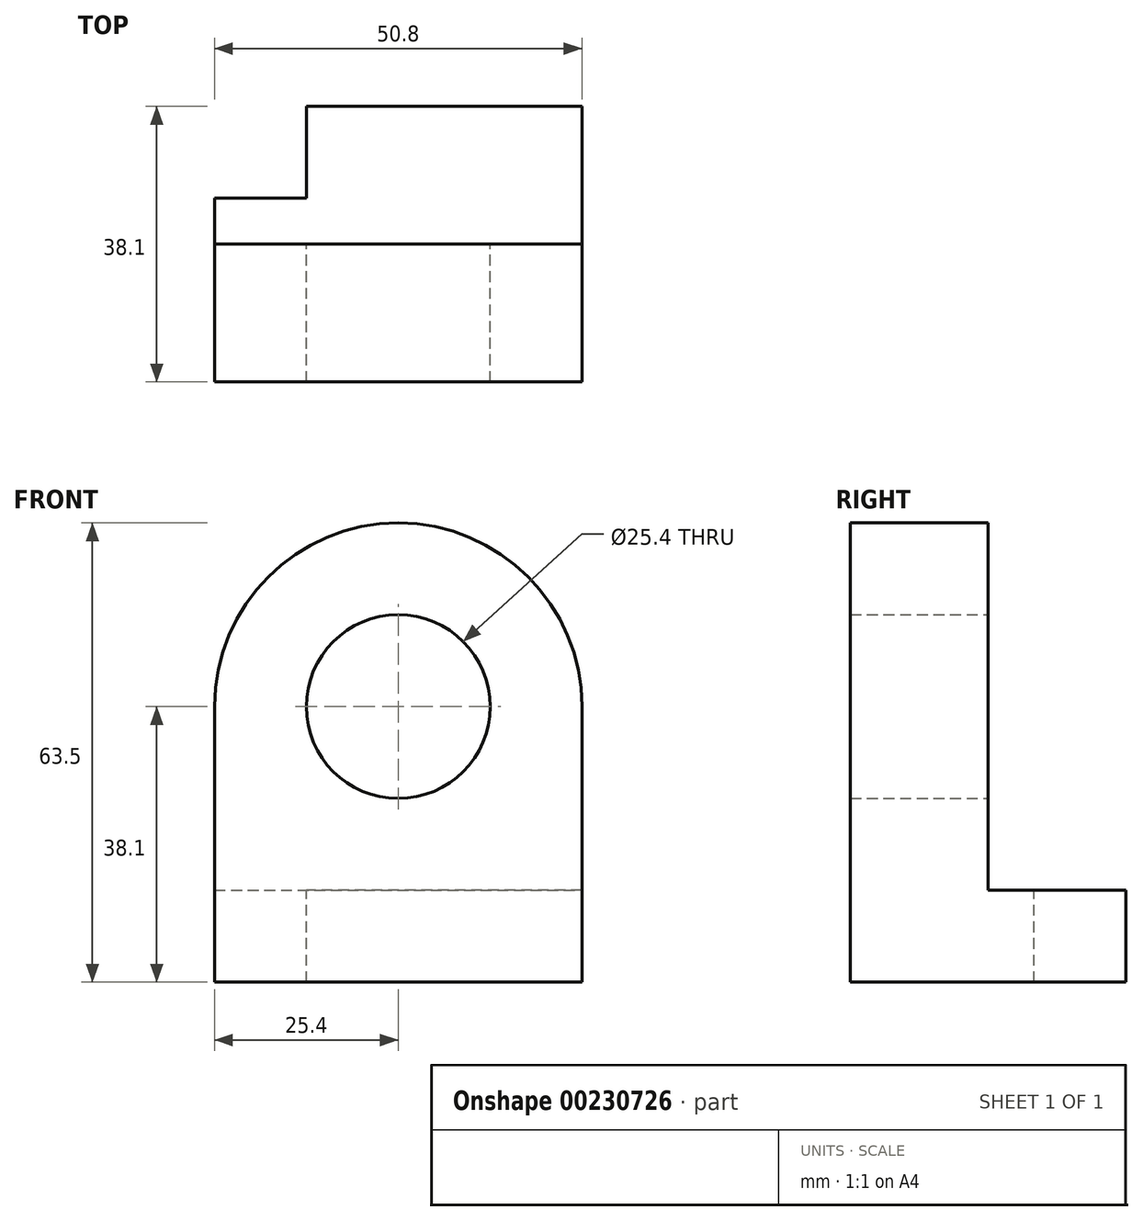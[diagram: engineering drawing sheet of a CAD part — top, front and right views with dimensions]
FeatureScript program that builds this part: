
annotation { "Feature Type Name" : "Feature", "Feature Type Description" : "" }
export const myFeature = defineFeature(function(context is Context, id is Id, definition is map)
    precondition{}
    {
        {
            var Q0;
            Q0=qCreatedBy(makeId("Top.planeOp"),FACE);
            var sketch = newSketch(context, id + "F0", { "sketchPlane" : qUnion([Q0])});
            skLineSegment(sketch, "E0.bottom", {"start": v(25.4, 19.05) * mm, "end": v(-25.4, 19.05) * mm});
            skLineSegment(sketch, "E0.top", {"start": v(25.4, -19.05) * mm, "end": v(-25.4, -19.05) * mm});
            skLineSegment(sketch, "E0.left", {"start": v(25.4, 19.05) * mm, "end": v(25.4, -19.05) * mm});
            skLineSegment(sketch, "E0.right", {"start": v(-25.4, 19.05) * mm, "end": v(-25.4, -19.05) * mm});
            skPoint(sketch, "E0.middle", {"position": v(0, 0) * mm});
            skSolve(sketch);
        }
        {
            var Q0;
            Q0=makeQuery(id+"F0.imprint","IMPRINT",FACE,{"disambiguationData":[TD([[makeQuery(id+"F0.imprint","IMPRINT",EDGE,{"derivedFrom":sQuery(id+"F0.wireOp",EDGE,"E0.bottom")}),1.0]])]});
            extrude(context, id + "F1", {"entities" : qUnion([Q0]), "endBound" : BoundingType.SYMMETRIC, "depth" : 12.7 * mm});
        }
        {
            var Q0;
            Q0=makeQuery(id+"F1.opExtrude","CAP_FACE",FACE,{"disambiguationData":[OSD([sQuery(id+"F0.wireOp",EDGE,"E0.bottom"),sQuery(id+"F0.wireOp",EDGE,"E0.top"),sQuery(id+"F0.wireOp",EDGE,"E0.left"),sQuery(id+"F0.wireOp",EDGE,"E0.right")])],"isStart":false});
            var sketch = newSketch(context, id + "F2", { "sketchPlane" : qUnion([Q0])});
            skLineSegment(sketch, "E1.bottom", {"start": v(-25.4, 19.05) * mm, "end": v(-12.7, 19.05) * mm});
            skLineSegment(sketch, "E1.top", {"start": v(-25.4, 6.35) * mm, "end": v(-12.7, 6.35) * mm});
            skLineSegment(sketch, "E1.left", {"start": v(-25.4, 19.05) * mm, "end": v(-25.4, 6.35) * mm});
            skLineSegment(sketch, "E1.right", {"start": v(-12.7, 19.05) * mm, "end": v(-12.7, 6.35) * mm});
            skSolve(sketch);
        }
        {
            var Q0;
            Q0=makeQuery(id+"F2.imprint","IMPRINT",FACE,{"disambiguationData":[TD([[makeQuery(id+"F2.imprint","IMPRINT",EDGE,{"derivedFrom":sQuery(id+"F2.wireOp",EDGE,"Q4ewAjpM-HIC3-mv71-0LCG-hEwrFqf2NVkZ.bottom")}),1.0]])]});
            var Q1;
            Q1=makeQuery(id+"F2.imprint","IMPRINT",FACE,{"disambiguationData":[TD([[makeQuery(id+"F2.imprint","IMPRINT",EDGE,{"derivedFrom":sQuery(id+"F2.wireOp",EDGE,"E1.bottom")}),1.0]])]});
            extrude(context, id + "F3", {"entities" : qUnion([Q0, Q1]), "operationType" : NewBodyOperationType.REMOVE, "endBound" : BoundingType.THROUGH_ALL, "oppositeDirection" : true, "depth" : 25.4 * mm});
        }
        {
            var Q0;
            Q0=makeQuery(id+"F1.opExtrude","CAP_FACE",FACE,{"disambiguationData":[OSD([sQuery(id+"F0.wireOp",EDGE,"E0.bottom"),sQuery(id+"F0.wireOp",EDGE,"E0.top"),sQuery(id+"F0.wireOp",EDGE,"E0.left"),sQuery(id+"F0.wireOp",EDGE,"E0.right")])],"isStart":false});
            var sketch = newSketch(context, id + "F4", { "sketchPlane" : qUnion([Q0])});
            skLineSegment(sketch, "E2.bottom", {"start": v(-25.4, -19.05) * mm, "end": v(25.4, -19.05) * mm});
            skLineSegment(sketch, "E2.top", {"start": v(-25.4, 0) * mm, "end": v(25.4, 0) * mm});
            skLineSegment(sketch, "E2.left", {"start": v(-25.4, -19.05) * mm, "end": v(-25.4, 0) * mm});
            skLineSegment(sketch, "E2.right", {"start": v(25.4, -19.05) * mm, "end": v(25.4, 0) * mm});
            skSolve(sketch);
        }
        {
            var Q0;
            Q0=makeQuery(id+"F4.imprint","IMPRINT",FACE,{"disambiguationData":[TD([[makeQuery(id+"F4.imprint","IMPRINT",EDGE,{"derivedFrom":sQuery(id+"F4.wireOp",EDGE,"E2.bottom")}),-1.0]])]});
            extrude(context, id + "F5", {"entities" : qUnion([Q0]), "operationType" : NewBodyOperationType.ADD, "depth" : 50.8 * mm});
        }
        {
            var Q0;
            Q0=makeQuery(id+"F5.opExtrude","SWEPT_FACE",FACE,{"disambiguationData":[OSD([sQuery(id+"F4.wireOp",EDGE,"E2.top")])]});
            var sketch = newSketch(context, id + "F6", { "sketchPlane" : qUnion([Q0])});
            skCircle(sketch, "E3", {"center": v(0, 31.75) * mm, "radius": 12.7 * mm});
            skCircle(sketch, "E4", {"center": v(0, 31.75) * mm, "radius": 25.4 * mm});
            skSolve(sketch);
        }
        {
            var Q0;
            {var subQ0=sQuery(id+"F6.wireOp",EDGE,"E4");var subQ1=sQuery(id+"F4.wireOp",EDGE,"E2.top");var subQ2=makeQuery(id+"F5.opExtrude","CAP_EDGE",EDGE,{"disambiguationData":[OSD([subQ1])],"isStart":false});var subQ3=makeQuery(id+"F6.imprint","INTERSECT",VERTEX,{"derivedFrom":[subQ2,subQ0]});Q0=makeQuery(id+"F6.imprint","IMPRINT",FACE,{"disambiguationData":[TD([[makeQuery(id+"F6.imprint","IMPRINT",EDGE,{"disambiguationData":[TD([[subQ3,-1.0]])],"derivedFrom":subQ0}),-1.0]])]});}
            var Q1;
            {var subQ0=sQuery(id+"F6.wireOp",EDGE,"E4");var subQ1=sQuery(id+"F4.wireOp",EDGE,"E2.top");var subQ2=makeQuery(id+"F5.opExtrude","CAP_EDGE",EDGE,{"disambiguationData":[OSD([subQ1])],"isStart":false});var subQ3=makeQuery(id+"F6.imprint","INTERSECT",VERTEX,{"derivedFrom":[subQ2,subQ0]});Q1=makeQuery(id+"F6.imprint","IMPRINT",FACE,{"disambiguationData":[TD([[makeQuery(id+"F6.imprint","IMPRINT",EDGE,{"disambiguationData":[TD([[subQ3,1.0]])],"derivedFrom":subQ0}),-1.0]])]});}
            extrude(context, id + "F7", {"entities" : qUnion([Q0, Q1]), "operationType" : NewBodyOperationType.REMOVE, "endBound" : BoundingType.THROUGH_ALL, "oppositeDirection" : true, "depth" : 25.4 * mm});
        }
        {
            var Q0;
            Q0=makeQuery(id+"F6.imprint","IMPRINT",FACE,{"disambiguationData":[TD([[makeQuery(id+"F6.imprint","IMPRINT",EDGE,{"derivedFrom":sQuery(id+"F6.wireOp",EDGE,"E3")}),1.0]])]});
            extrude(context, id + "F8", {"entities" : qUnion([Q0]), "operationType" : NewBodyOperationType.REMOVE, "endBound" : BoundingType.THROUGH_ALL, "oppositeDirection" : true, "depth" : 25.4 * mm});
        }
    });
